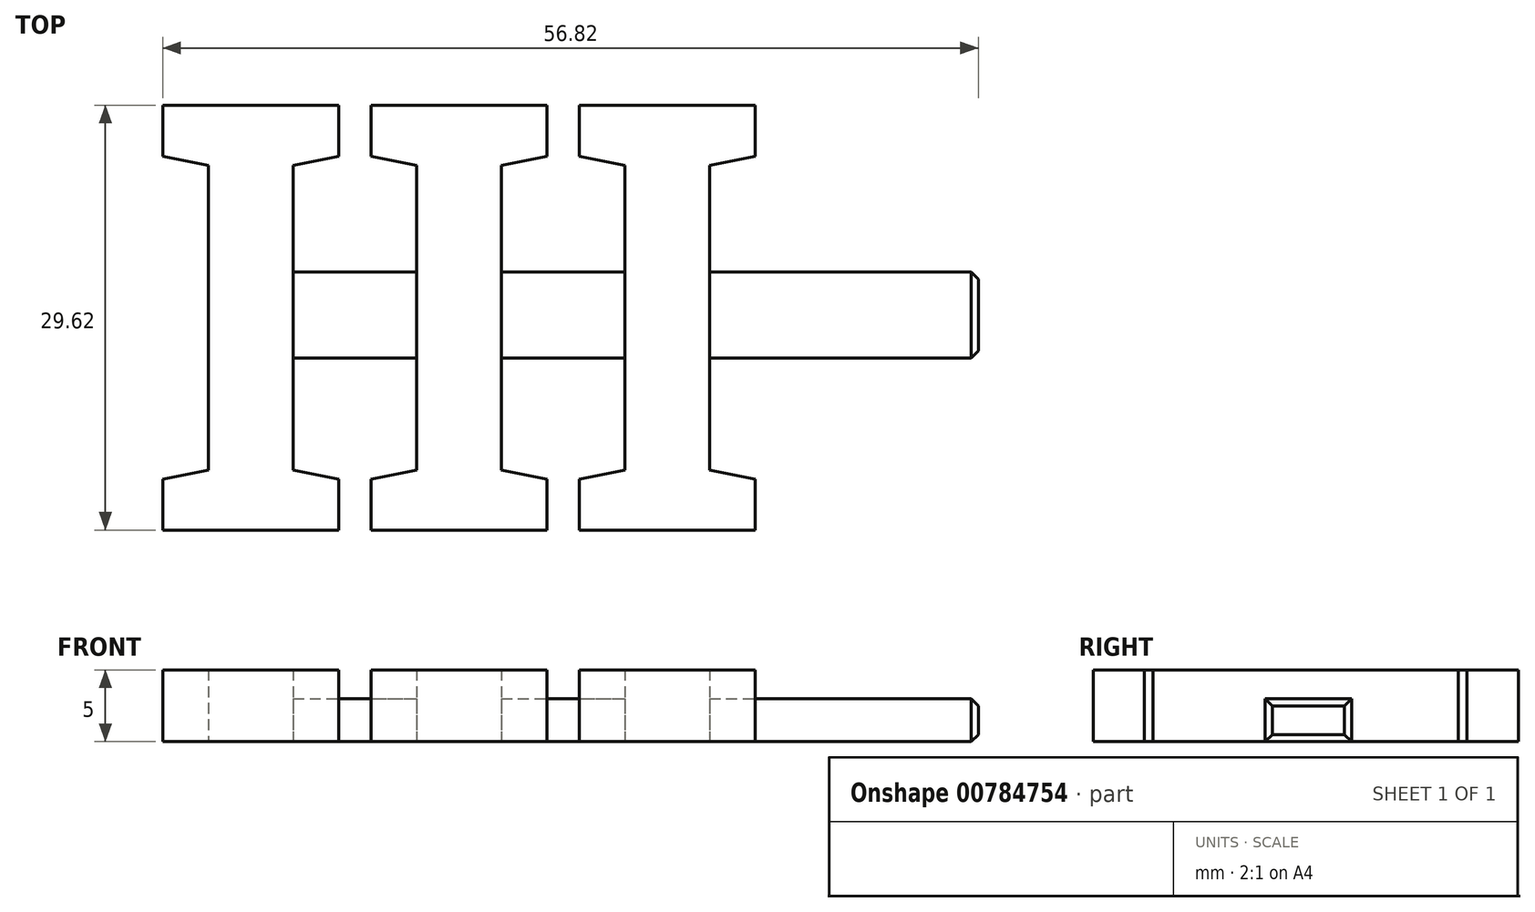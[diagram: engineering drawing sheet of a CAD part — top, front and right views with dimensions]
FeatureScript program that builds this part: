
annotation { "Feature Type Name" : "Feature", "Feature Type Description" : "" }
export const myFeature = defineFeature(function(context is Context, id is Id, definition is map)
    precondition{}
    {
        {
            var Q0;
            Q0=qCreatedBy(makeId("Top.planeOp"),FACE);
            var sketch = newSketch(context, id + "F0", { "sketchPlane" : qUnion([Q0])});
            skLineSegment(sketch, "E0.bottom", {"start": v(-15.03, 15) * mm, "end": v(15.03, 15) * mm, "construction": true});
            skLineSegment(sketch, "E0.left", {"start": v(-15.03, 15) * mm, "end": v(-15.03, 0) * mm, "construction": true});
            skLineSegment(sketch, "E0.right", {"start": v(15.03, 15) * mm, "end": v(15.03, -7.5) * mm, "construction": true});
            skText(sketch, "E1", { "text": "III", "fontName": "RobotoSlab-Bold.ttf"});
            skLineSegment(sketch, "E2.bottom", {"start": v(-12.5, 3) * mm, "end": v(12.5, 3) * mm});
            skLineSegment(sketch, "E2.top", {"start": v(-12.5, -3) * mm, "end": v(12.5, -3) * mm});
            skLineSegment(sketch, "E3.bottom", {"start": v(12.5, 3) * mm, "end": v(35.47, 3) * mm});
            skLineSegment(sketch, "E3.top", {"start": v(12.5, -3) * mm, "end": v(35.47, -3) * mm});
            skLineSegment(sketch, "E3.right", {"start": v(35.47, 3) * mm, "end": v(35.47, -3) * mm});
            const initialGuessF0  = {"E1": [-0.02247, -0.015, 1, 0, 0.03]};
            skSetInitialGuess(sketch, initialGuessF0);
            skSolve(sketch);
        }
        {
            var Q0;
            Q0=makeQuery(id+"F0.imprint","IMPRINT",FACE,{"disambiguationData":[TD([[makeQuery(id+"F0.imprint","IMPRINT",EDGE,{"derivedFrom":sQuery(id+"F0.wireOp",EDGE,"E1.sketch_text.stroke-0")}),-1.0]])]});
            var Q1;
            Q1=makeQuery(id+"F0.imprint","IMPRINT",FACE,{"disambiguationData":[TD([[makeQuery(id+"F0.imprint","IMPRINT",EDGE,{"derivedFrom":sQuery(id+"F0.wireOp",EDGE,"E1.sketch_text.stroke-12")}),-1.0]])]});
            var Q2;
            {var subQ0=sQuery(id+"F0.wireOp",EDGE,"E2.bottom");var subQ1=sQuery(id+"F0.wireOp",EDGE,"E1.sketch_text.stroke-16");var subQ2=makeQuery(id+"F0.imprint","INTERSECT",VERTEX,{"derivedFrom":[subQ1,subQ0]});Q2=makeQuery(id+"F0.imprint","IMPRINT",FACE,{"disambiguationData":[TD([[makeQuery(id+"F0.imprint","IMPRINT",EDGE,{"disambiguationData":[TD([[subQ2,-1.0]])],"derivedFrom":subQ1}),-1.0]])]});}
            var Q3;
            {var subQ0=sQuery(id+"F0.wireOp",EDGE,"E1.sketch_text.stroke-17");Q3=makeQuery(id+"F0.imprint","IMPRINT",FACE,{"disambiguationData":[TD([[makeQuery(id+"F0.imprint","IMPRINT",EDGE,{"derivedFrom":subQ0}),-1.0]])]});}
            var Q4;
            Q4=makeQuery(id+"F0.imprint","IMPRINT",FACE,{"disambiguationData":[TD([[makeQuery(id+"F0.imprint","IMPRINT",EDGE,{"derivedFrom":sQuery(id+"F0.wireOp",EDGE,"E1.sketch_text.stroke-24")}),-1.0]])]});
            var Q5;
            {var subQ0=sQuery(id+"F0.wireOp",EDGE,"E3.bottom");var subQ9=sQuery(id+"F0.wireOp",EDGE,"E1.sketch_text.stroke-28");var subQ10=makeQuery(id+"F0.imprint","INTERSECT",VERTEX,{"derivedFrom":[subQ9,subQ0]});Q5=makeQuery(id+"F0.imprint","IMPRINT",FACE,{"disambiguationData":[TD([[makeQuery(id+"F0.imprint","IMPRINT",EDGE,{"disambiguationData":[TD([[subQ10,-1.0]])],"derivedFrom":subQ9}),-1.0]])]});}
            var Q6;
            {var subQ0=sQuery(id+"F0.wireOp",EDGE,"E1.sketch_text.stroke-29");Q6=makeQuery(id+"F0.imprint","IMPRINT",FACE,{"disambiguationData":[TD([[makeQuery(id+"F0.imprint","IMPRINT",EDGE,{"derivedFrom":subQ0}),-1.0]])]});}
            extrude(context, id + "F1", {"entities" : qUnion([Q0, Q1, Q2, Q3, Q4, Q5, Q6]), "depth" : 5 * mm, "offsetDistance" : 25 * mm});
        }
        {
            var Q0;
            {var subQ0=sQuery(id+"F0.wireOp",EDGE,"E2.bottom");var subQ1=sQuery(id+"F0.wireOp",EDGE,"E1.sketch_text.stroke-4");var subQ2=makeQuery(id+"F0.imprint","INTERSECT",VERTEX,{"derivedFrom":[subQ1,subQ0]});Q0=makeQuery(id+"F0.imprint","IMPRINT",FACE,{"disambiguationData":[TD([[makeQuery(id+"F0.imprint","IMPRINT",EDGE,{"disambiguationData":[TD([[subQ2,-1.0]])],"derivedFrom":subQ1}),1.0]])]});}
            var Q1;
            {var subQ0=sQuery(id+"F0.wireOp",EDGE,"E2.bottom");var subQ1=sQuery(id+"F0.wireOp",EDGE,"E1.sketch_text.stroke-16");var subQ2=makeQuery(id+"F0.imprint","INTERSECT",VERTEX,{"derivedFrom":[subQ1,subQ0]});Q1=makeQuery(id+"F0.imprint","IMPRINT",FACE,{"disambiguationData":[TD([[makeQuery(id+"F0.imprint","IMPRINT",EDGE,{"disambiguationData":[TD([[subQ2,-1.0]])],"derivedFrom":subQ1}),1.0]])]});}
            var Q2;
            {var subQ5=sQuery(id+"F0.wireOp",EDGE,"E3.right");Q2=makeQuery(id+"F0.imprint","IMPRINT",FACE,{"disambiguationData":[TD([[makeQuery(id+"F0.imprint","IMPRINT",EDGE,{"derivedFrom":subQ5}),-1.0]])]});}
            extrude(context, id + "F2", {"entities" : qUnion([Q0, Q1, Q2]), "operationType" : NewBodyOperationType.ADD, "depth" : 3 * mm, "offsetDistance" : 25 * mm});
        }
        {
            var Q0;
            Q0=makeQuery(id+"F2.opExtrude","CAP_EDGE",EDGE,{"disambiguationData":[OSD([sQuery(id+"F0.wireOp",EDGE,"E3.right")])],"isStart":false});
            var Q1;
            Q1=makeQuery(id+"F2.opExtrude","SWEPT_EDGE",EDGE,{"disambiguationData":[OSD([sQuery(id+"F0.wireOp",EDGE,"E3.bottom"),sQuery(id+"F0.wireOp",EDGE,"E3.right")])]});
            var Q2;
            Q2=makeQuery(id+"F2.opExtrude","CAP_EDGE",EDGE,{"disambiguationData":[OSD([sQuery(id+"F0.wireOp",EDGE,"E3.right")])],"isStart":true});
            var Q3;
            Q3=makeQuery(id+"F2.opExtrude","SWEPT_EDGE",EDGE,{"disambiguationData":[OSD([sQuery(id+"F0.wireOp",EDGE,"E3.top"),sQuery(id+"F0.wireOp",EDGE,"E3.right")])]});
            chamfer(context, id + "F3", {"entities" : qUnion([Q0, Q1, Q2, Q3]), "width" : 0.5 * mm, "tangentPropagation" : true});
        }
    });
